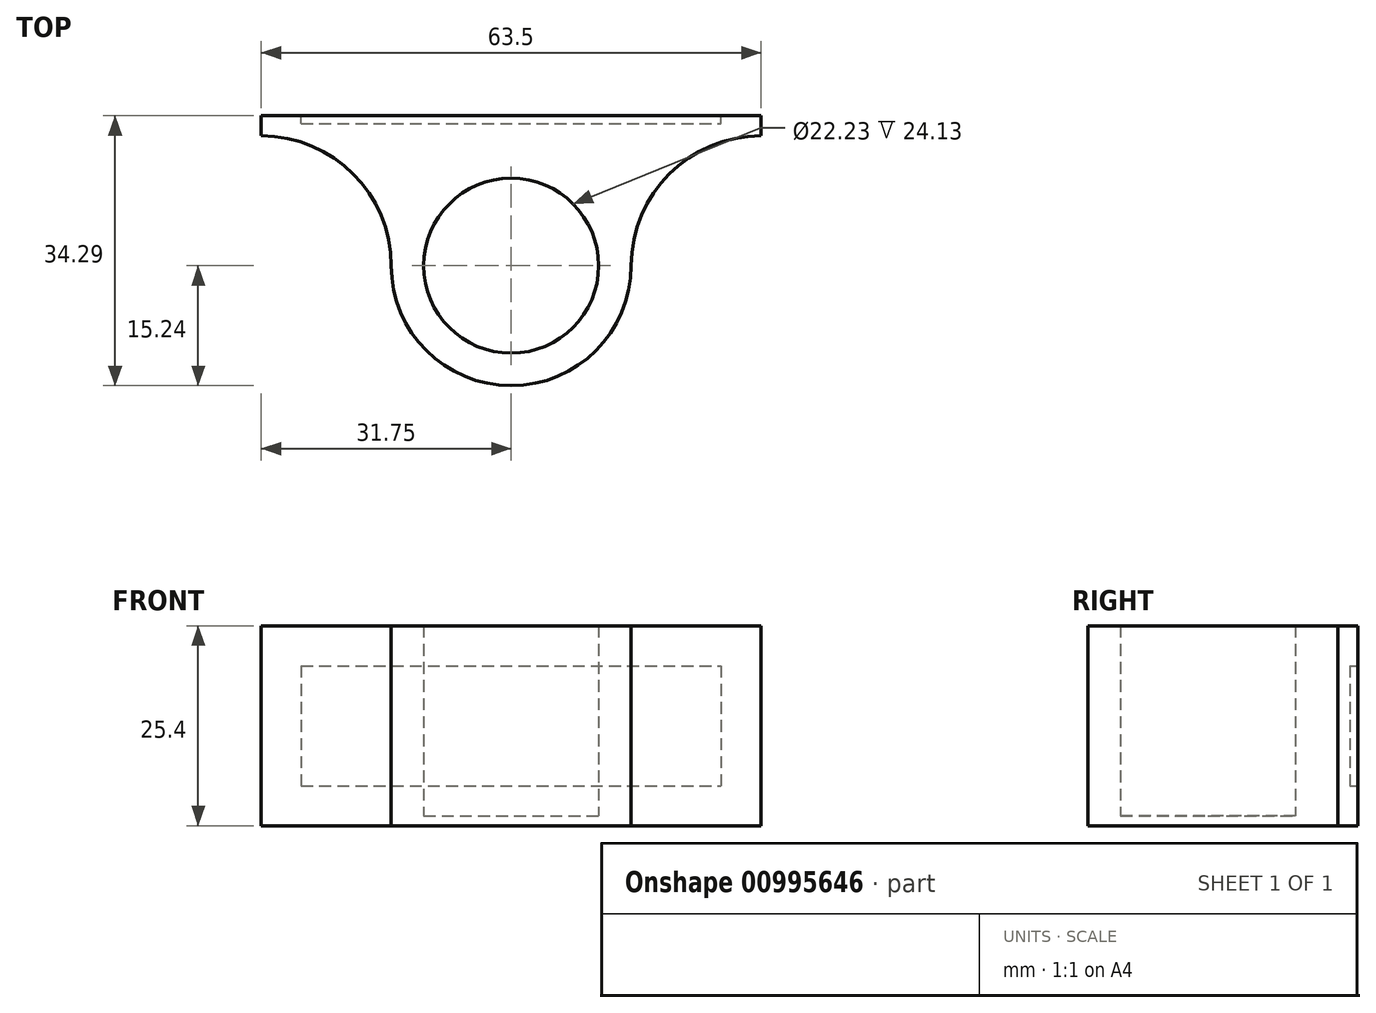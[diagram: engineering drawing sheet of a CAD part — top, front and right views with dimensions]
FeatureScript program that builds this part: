
annotation { "Feature Type Name" : "Feature", "Feature Type Description" : "" }
export const myFeature = defineFeature(function(context is Context, id is Id, definition is map)
    precondition{}
    {
        {
            var Q0;
            Q0=qCreatedBy(makeId("Top.planeOp"),FACE);
            var sketch = newSketch(context, id + "F0", { "sketchPlane" : qUnion([Q0])});
            skCircle(sketch, "E0", {"center": v(0, 0) * mm, "radius": 11.11 * mm});
            skArc(sketch, "E1", {"start": v(-15.24, 0) * mm, "mid": v(0, -15.24) * mm, "end": v(15.24, 0) * mm});
            skArc(sketch, "E2", {"start": v(-15.24, 0) * mm, "mid": v(-20.08, 11.67) * mm, "end": v(-31.75, 16.51) * mm});
            skArc(sketch, "E3", {"start": v(31.75, 16.51) * mm, "mid": v(20.08, 11.67) * mm, "end": v(15.24, 0) * mm});
            skLineSegment(sketch, "E4", {"start": v(-31.75, 16.51) * mm, "end": v(-31.75, 19.05) * mm});
            skLineSegment(sketch, "E5", {"start": v(-31.75, 19.05) * mm, "end": v(31.75, 19.05) * mm});
            skLineSegment(sketch, "E6", {"start": v(31.75, 19.05) * mm, "end": v(31.75, 16.51) * mm});
            skSolve(sketch);
        }
        {
            var Q0;
            Q0 = qSketchRegion(id + "F0", true);
            extrude(context, id + "F1", {"entities" : qUnion([Q0]), "depth" : 25.4 * mm, "offsetDistance" : 25.4 * mm});
        }
        {
            var Q0;
            Q0=makeQuery(id+"F1.opExtrude","CAP_FACE",FACE,{"disambiguationData":[OSD([sQuery(id+"F0.wireOp",EDGE,"E0"),sQuery(id+"F0.wireOp",EDGE,"E1"),sQuery(id+"F0.wireOp",EDGE,"E2"),sQuery(id+"F0.wireOp",EDGE,"E3"),sQuery(id+"F0.wireOp",EDGE,"E4"),sQuery(id+"F0.wireOp",EDGE,"E5"),sQuery(id+"F0.wireOp",EDGE,"E6")])],"isStart":true});
            var sketch = newSketch(context, id + "F2", { "sketchPlane" : qUnion([Q0])});
            skCircle(sketch, "E7", {"center": v(0, 0) * mm, "radius": 15.24 * mm});
            skSolve(sketch);
        }
        {
            var Q0;
            Q0 = qSketchRegion(id + "F2", true);
            extrude(context, id + "F3", {"entities" : qUnion([Q0]), "operationType" : NewBodyOperationType.ADD, "oppositeDirection" : true, "depth" : 1.27 * mm, "offsetDistance" : 25.4 * mm});
        }
        {
            var Q0;
            Q0=makeQuery(id+"F1.opExtrude","SWEPT_FACE",FACE,{"disambiguationData":[OSD([sQuery(id+"F0.wireOp",EDGE,"E5")])]});
            var sketch = newSketch(context, id + "F4", { "sketchPlane" : qUnion([Q0])});
            skLineSegment(sketch, "E8.0", {"start": v(26.67, 20.32) * mm, "end": v(-26.67, 20.32) * mm});
            skLineSegment(sketch, "E8.1", {"start": v(26.67, 20.32) * mm, "end": v(26.67, 5.08) * mm});
            skLineSegment(sketch, "E8.2", {"start": v(26.67, 5.08) * mm, "end": v(-26.67, 5.08) * mm});
            skLineSegment(sketch, "E8.3", {"start": v(-26.67, 20.32) * mm, "end": v(-26.67, 5.08) * mm});
            skSolve(sketch);
        }
        {
            var Q0;
            Q0 = qSketchRegion(id + "F4", true);
            extrude(context, id + "F5", {"entities" : qUnion([Q0]), "operationType" : NewBodyOperationType.REMOVE, "oppositeDirection" : true, "depth" : 1.02 * mm, "offsetDistance" : 25.4 * mm});
        }
    });
